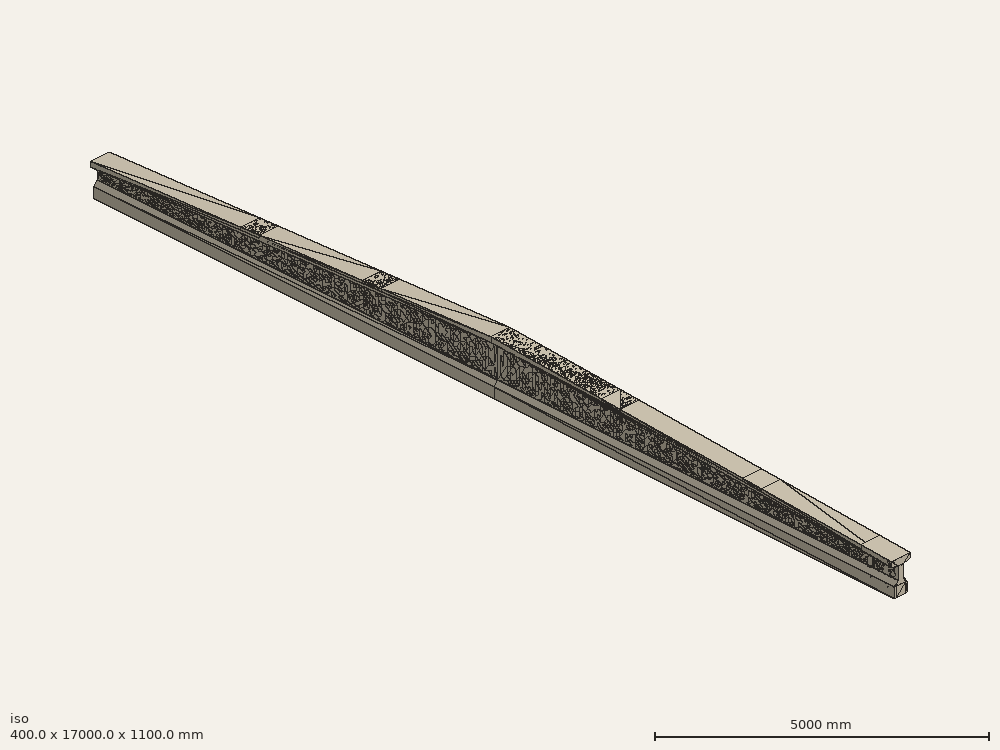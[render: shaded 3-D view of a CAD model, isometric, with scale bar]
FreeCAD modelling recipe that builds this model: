
FCSTD DOCUMENT  (FreeCAD 0.21R33694 (Git))
Label: LGH_3002_beam
License: All rights reserved
LicenseURL: http://en.wikipedia.org/wiki/All_rights_reserved
objects: Part::FeaturePython×24, Part::Feature×20, Part::Part2DObjectPython×9, Fem::ConstraintForce×9, Sketcher::SketchObject×6, App::MaterialObjectPython×4, Part::Extrusion×3, Part::Compound×3, Part::Mirroring×2, Fem::ConstraintDisplacement×2, Part::Loft×1, App::DocumentObjectGroup×1, Fem::FemSolverObjectPython×1, Fem::FemMeshObjectPython×1, Fem::FemAnalysis×1
note: 68 computed .brp shape members not serialized (recipe doc carries the construction recipe); baked Part::Feature solids carry a one-line shape summary decoded from their .brp

FEATURE [Sketcher::SketchObject] Sketch
  FullyConstrained = true
  Placement = pos=(0,0,0) rot=(1,0,0;1.5708rad)
  sketch-geometry (12):
    g0: LineSegment StartX=-130 StartY=0 StartZ=0 EndX=130 EndY=4e-16 EndZ=0
    g1: LineSegment StartX=130 StartY=4e-16 StartZ=0 EndX=130 EndY=200 EndZ=0
    g2: LineSegment StartX=130 StartY=200 StartZ=0 EndX=60 EndY=290 EndZ=0
    g3: LineSegment StartX=60 StartY=290 StartZ=0 EndX=60 EndY=540 EndZ=0
    g4: LineSegment StartX=60 StartY=540 StartZ=0 EndX=200 EndY=570 EndZ=0
    g5: LineSegment StartX=200 StartY=570 StartZ=0 EndX=200 EndY=670 EndZ=0
    g6: LineSegment StartX=200 StartY=670 StartZ=0 EndX=-200 EndY=670 EndZ=0
    g7: LineSegment StartX=-200 StartY=670 StartZ=0 EndX=-200 EndY=570 EndZ=0
    g8: LineSegment StartX=-200 StartY=570 StartZ=0 EndX=-60 EndY=540 EndZ=0
    g9: LineSegment StartX=-60 StartY=540 StartZ=0 EndX=-60 EndY=290 EndZ=0
    g10: LineSegment StartX=-60 StartY=290 StartZ=0 EndX=-130 EndY=200 EndZ=0
    g11: LineSegment StartX=-130 StartY=200 StartZ=0 EndX=-130 EndY=0 EndZ=0
  constraints (33):
    c: PointOnObject(g0,g-1)
    c: Symmetric(g0,g0,g-2)
    c: DistanceX(g0,g0) = 260
    c: Coincident(g0,g1)
    c: Vertical(g1)
    c: Coincident(g1,g2)
    c: Coincident(g2,g3)
    c: Vertical(g3)
    c: Coincident(g3,g4)
    c: Coincident(g4,g5)
    c: Vertical(g5)
    c: Coincident(g5,g6)
    c: Coincident(g6,g7)
    c: Vertical(g7)
    c: Coincident(g7,g8)
    c: Coincident(g8,g9)
    c: Vertical(g9)
    c: Coincident(g9,g10)
    c: Coincident(g10,g11)
    c: Coincident(g11,g0)
    c: Vertical(g11)
    c: Equal(g11,g1)
    c: Symmetric(g9,g2,g-2)
    c: Equal(g9,g3)
    c: Symmetric(g6,g5,g-2)
    c: DistanceX(g6,g6) = 400
    c: DistanceY(g0,g5) = 670
    c: Equal(g7,g5)
    c: DistanceX(g9,g2) = 120
    c: DistanceY(g5,g5) = 100
    c: DistanceY(g3,g4) = 30
    c: DistanceY(g1,g1) = 200
    c: DistanceY(g1,g2) = 90
FEATURE [Sketcher::SketchObject] Sketch001
  FullyConstrained = true
  Placement = pos=(0,8500,0) rot=(1,0,0;1.5708rad)
  sketch-geometry (12):
    g0: LineSegment StartX=-130 StartY=0 StartZ=0 EndX=130 EndY=0 EndZ=0
    g1: LineSegment StartX=130 StartY=0 StartZ=0 EndX=130 EndY=200 EndZ=0
    g2: LineSegment StartX=130 StartY=200 StartZ=0 EndX=60 EndY=290 EndZ=0
    g3: LineSegment StartX=60 StartY=290 StartZ=0 EndX=60 EndY=970 EndZ=0
    g4: LineSegment StartX=60 StartY=970 StartZ=0 EndX=200 EndY=1000 EndZ=0
    g5: LineSegment StartX=200 StartY=1000 StartZ=0 EndX=200 EndY=1100 EndZ=0
    g6: LineSegment StartX=200 StartY=1100 StartZ=0 EndX=-200 EndY=1100 EndZ=0
    g7: LineSegment StartX=-200 StartY=1100 StartZ=0 EndX=-200 EndY=1000 EndZ=0
    g8: LineSegment StartX=-200 StartY=1000 StartZ=0 EndX=-60 EndY=970 EndZ=0
    g9: LineSegment StartX=-60 StartY=970 StartZ=0 EndX=-60 EndY=290 EndZ=0
    g10: LineSegment StartX=-60 StartY=290 StartZ=0 EndX=-130 EndY=200 EndZ=0
    g11: LineSegment StartX=-130 StartY=200 StartZ=0 EndX=-130 EndY=0 EndZ=0
  constraints (33):
    c: PointOnObject(g0,g-1)
    c: Symmetric(g0,g0,g-2)
    c: DistanceX(g0,g0) = 260
    c: Coincident(g0,g1)
    c: Vertical(g1)
    c: Coincident(g1,g2)
    c: Coincident(g2,g3)
    c: Vertical(g3)
    c: Coincident(g3,g4)
    c: Coincident(g4,g5)
    c: Vertical(g5)
    c: Coincident(g5,g6)
    c: Coincident(g6,g7)
    c: Vertical(g7)
    c: Coincident(g7,g8)
    c: Coincident(g8,g9)
    c: Vertical(g9)
    c: Coincident(g9,g10)
    c: Coincident(g10,g11)
    c: Coincident(g11,g0)
    c: Vertical(g11)
    c: Equal(g11,g1)
    c: Symmetric(g9,g2,g-2)
    c: Equal(g9,g3)
    c: Symmetric(g6,g5,g-2)
    c: DistanceX(g6,g6) = 400
    c: DistanceY(g0,g5) = 1100
    c: Equal(g7,g5)
    c: DistanceX(g9,g2) = 120
    c: DistanceY(g5,g5) = 100
    c: DistanceY(g3,g4) = 30
    c: DistanceY(g1,g1) = 200
    c: DistanceY(g1,g2) = 90
FEATURE [Part::Loft] Loft
  Closed = false
  MaxDegree = 5
  Ruled = false
  Sections = -> [Sketch,Sketch001]
  Solid = true
FEATURE [Part::Part2DObjectPython] Rectangle  # Draft 2D object (typed FeaturePython)
  Area = 3.16759e+06
  ChamferSize = 0
  Columns = 1
  FilletRadius = 0
  Height = 1690
  Length = 1874.31
  MakeFace = true
  Placement = pos=(-1011.48,650,-530.33) rot=(1,0,0;1.5708rad)
  Rows = 1
FEATURE [Part::Feature] Loft001
  Placement = pos=(1.041e-12,17000,0) rot=(0,0,1;3.14159rad)
  shape: bbox 400 x 8500 x 1100 mm, 14 faces (baked)
FEATURE [Part::Feature] Loft002
  shape: bbox 400 x 8500 x 1100 mm, 14 faces (baked)
FEATURE [Part::FeaturePython] Slice  # WARN: FeaturePython — macro-defined, semantics opaque (R4)
  Base = -> Loft002
  Mode = 1
  Tolerance = 0
  Tools = -> [Rectangle]
FEATURE [Part::FeaturePython] Slice_child0  label="Slice.0"  # WARN: FeaturePython — macro-defined, semantics opaque (R4)
  Base = -> Slice
  FilterType = 1
  Invert = false
  OverrideMaxVal = 0
  WindowFrom = 80
  WindowTo = 100
  items = 0
FEATURE [Part::FeaturePython] Slice_child1  label="Slice.1"  # WARN: FeaturePython — macro-defined, semantics opaque (R4)
  Base = -> Slice
  FilterType = 1
  Invert = false
  OverrideMaxVal = 0
  WindowFrom = 80
  WindowTo = 100
  items = 1
FEATURE [App::DocumentObjectGroup] GrExplode_Slice  label="Exploded Slice"
  Group = -> [Slice_child0,Slice_child1]
FEATURE [Part::FeaturePython] Facebinder  # WARN: FeaturePython — macro-defined, semantics opaque (R4)
  Area = 150846
  Extrusion = 0
  Faces = -> [Slice_child1]
  RemoveSplitter = false
  Sew = false
FEATURE [Sketcher::SketchObject] Sketch002  label="Lage_Spannkabel"
  FullyConstrained = false
  MapMode = 5
  Placement = pos=(0,650,0) rot=(1,0,0;1.5708rad)
  Support = -> [Facebinder]
  sketch-geometry (2):
    g0: LineSegment StartX=0 StartY=0 StartZ=0 EndX=0 EndY=362 EndZ=0
    g1: LineSegment StartX=0 StartY=100 StartZ=0 EndX=947.371 EndY=100 EndZ=0
  constraints (6):
    c: Coincident(g0,g-1)
    c: Vertical(g0)
    c: DistanceY(g0,g0) = 362
    c: PointOnObject(g1,g0)
    c: Horizontal(g1)
    c: DistanceY(g1,g0) = 262
FEATURE [Sketcher::SketchObject] Sketch003
  ExternalGeometry = -> [Sketch002]
  FullyConstrained = true
  MapMode = 5
  Placement = pos=(0,0,0) rot=(1,0,0;1.5708rad)
  Support = -> [Loft]
  sketch-geometry (4):
    g0: LineSegment StartX=-100 StartY=200 StartZ=0 EndX=100 EndY=200 EndZ=0
    g1: LineSegment StartX=100 StartY=200 StartZ=0 EndX=100 EndY=0 EndZ=0
    g2: LineSegment StartX=100 StartY=0 StartZ=0 EndX=-100 EndY=0 EndZ=0
    g3: LineSegment StartX=-100 StartY=0 StartZ=0 EndX=-100 EndY=200 EndZ=0
  constraints (10):
    c: Coincident(g0,g1)
    c: Coincident(g1,g2)
    c: Coincident(g2,g3)
    c: Coincident(g3,g0)
    c: Horizontal(g0)
    c: Vertical(g3)
    c: Symmetric(g1,g0,g-3)
    c: Symmetric(g2,g1,g-2)
    c: DistanceX(g2,g2) = 200
    c: PointOnObject(g1,g-1)
FEATURE [Part::Extrusion] Extrude  label="Lager_links"
  Base = -> Sketch003
  Dir = (0,1,0)
  DirMode = 0
  FaceMakerClass = Part::FaceMakerBullseye
  LengthFwd = 200
  LengthRev = 0
  Solid = true
  Symmetric = false
FEATURE [Part::FeaturePython] Clone  label="Lager_rechts"  # Draft clone (typed FeaturePython)
  AttacherType = Attacher::AttachEngine3D
  Fuse = false
  Objects = -> [Extrude]
  Placement = pos=(1.0409e-12,16800,2e-16) rot=(0,0,1;0rad)
  Scale = (1,1,1)
FEATURE [Sketcher::SketchObject] Sketch004
  ExternalGeometry = -> [Loft]
  FullyConstrained = true
  MapMode = 5
  Placement = pos=(0,-33.8076,668.29) rot=(1,0,0;0.050545rad)
  Support = -> [Loft]
  sketch-geometry (12):
    g0: LineSegment StartX=-200 StartY=6200 StartZ=0 EndX=200 EndY=6200 EndZ=0
    g1: LineSegment StartX=200 StartY=6200 StartZ=0 EndX=200 EndY=5800 EndZ=0
    g2: LineSegment StartX=200 StartY=5800 StartZ=0 EndX=-200 EndY=5800 EndZ=0
    g3: LineSegment StartX=-200 StartY=5800 StartZ=0 EndX=-200 EndY=6200 EndZ=0
    g4: LineSegment StartX=-200 StartY=3200 StartZ=0 EndX=200 EndY=3200 EndZ=0
    g5: LineSegment StartX=200 StartY=3200 StartZ=0 EndX=200 EndY=2800 EndZ=0
    g6: LineSegment StartX=200 StartY=2800 StartZ=0 EndX=-200 EndY=2800 EndZ=0
    g7: LineSegment StartX=-200 StartY=2800 StartZ=0 EndX=-200 EndY=3200 EndZ=0
    g8: LineSegment StartX=-200 StartY=5800 StartZ=0 EndX=0 EndY=6000 EndZ=0
    g9: LineSegment StartX=0 StartY=6000 StartZ=0 EndX=200 EndY=6200 EndZ=0
    g10: LineSegment StartX=-200 StartY=2800 StartZ=0 EndX=0 EndY=3000 EndZ=0
    g11: LineSegment StartX=0 StartY=3000 StartZ=0 EndX=200 EndY=3200 EndZ=0
  constraints (32):
    c: Coincident(g0,g1)
    c: Coincident(g1,g2)
    c: Coincident(g2,g3)
    c: Coincident(g3,g0)
    c: Horizontal(g0)
    c: Vertical(g1)
    c: Vertical(g3)
    c: Coincident(g4,g5)
    c: Coincident(g5,g6)
    c: Coincident(g6,g7)
    c: Coincident(g7,g4)
    c: Horizontal(g4)
    c: Vertical(g5)
    c: Vertical(g7)
    c: Symmetric(g2,g1,g-2)
    c: DistanceX(g2,g2) = 400
    c: Symmetric(g6,g5,g-2)
    c: Equal(g2,g6)
    c: Coincident(g2,g8)
    c: PointOnObject(g8,g-2)
    c: Coincident(g8,g9)
    c: Coincident(g9,g0)
    c: Coincident(g6,g10)
    c: PointOnObject(g10,g-2)
    c: Coincident(g11,g10)
    c: Coincident(g11,g4)
    c: Parallel(g10,g11)
    c: Equal(g6,g5)
    c: Parallel(g8,g9)
    c: Equal(g2,g1)
    c: DistanceY(g10,g8) = 3000
    c: DistanceY(g-1,g10) = 3000
FEATURE [Part::Extrusion] Extrude001  label="Auflager_Mast"
  Base = -> Sketch004
  Dir = (0,-0.0505236,0.998723)
  DirMode = 2
  FaceMakerClass = Part::FaceMakerBullseye
  LengthFwd = 50
  LengthRev = 0
  Reversed = true
  Solid = true
  Symmetric = false
FEATURE [Sketcher::SketchObject] Sketch005
  ExternalGeometry = -> [Extrude001,Loft001]
  FullyConstrained = true
  MapMode = 5
  Placement = pos=(1.041e-12,17033.8,668.29) rot=(0,0.02527,0.999681;3.14159rad)
  Support = -> [Loft001]
  sketch-geometry (8):
    g0: LineSegment StartX=-200 StartY=3227.29 StartZ=0 EndX=200 EndY=3227.29 EndZ=0
    g1: LineSegment StartX=200 StartY=3227.29 StartZ=0 EndX=200 EndY=3627.29 EndZ=0
    g2: LineSegment StartX=200 StartY=3627.29 StartZ=0 EndX=-200 EndY=3627.29 EndZ=0
    g3: LineSegment StartX=-200 StartY=3627.29 StartZ=0 EndX=-200 EndY=3227.29 EndZ=0
    g4: LineSegment StartX=-200 StartY=6211.97 StartZ=0 EndX=200 EndY=6211.97 EndZ=0
    g5: LineSegment StartX=200 StartY=6211.97 StartZ=0 EndX=200 EndY=5811.97 EndZ=0
    g6: LineSegment StartX=200 StartY=5811.97 StartZ=0 EndX=-200 EndY=5811.97 EndZ=0
    g7: LineSegment StartX=-200 StartY=5811.97 StartZ=0 EndX=-200 EndY=6211.97 EndZ=0
  constraints (22):
    c: Coincident(g0,g1)
    c: Coincident(g1,g2)
    c: Coincident(g2,g3)
    c: Coincident(g3,g0)
    c: Horizontal(g0)
    c: Horizontal(g2)
    c: Vertical(g1)
    c: Vertical(g3)
    c: Coincident(g4,g5)
    c: Coincident(g5,g6)
    c: Coincident(g6,g7)
    c: Coincident(g7,g4)
    c: Horizontal(g4)
    c: Horizontal(g6)
    c: Vertical(g5)
    c: Vertical(g7)
    c: Symmetric(g0,g-3,g-5)
    c: Vertical(g0,g-5)
    c: Vertical(g-5,g4)
    c: Symmetric(g4,g-4,g-5)
    c: Equal(g6,g7)
    c: Equal(g7,g3)
FEATURE [Part::Extrusion] Extrude002  label="Auflager_dummy"
  Base = -> Sketch005
  Dir = (0,0.0505236,0.998723)
  DirMode = 2
  FaceMakerClass = Part::FaceMakerBullseye
  LengthFwd = 50
  LengthRev = 0
  Reversed = true
  Solid = true
  Symmetric = false
FEATURE [Fem::FemSolverObjectPython] SolverCcxTools  # FEM object (typed FeaturePython)
  AnalysisType = 0
  BeamShellResultOutput3D = true
  BucklingFactors = 1
  EigenmodeHighLimit = 1000000
  EigenmodeLowLimit = 0
  EigenmodesCount = 10
  GeometricalNonlinearity = 0
  IterationsControlParameterCutb = 0.25,0.5,0.75,0.85,,,1.5,
  IterationsControlParameterIter = 4,8,9,200,10,400,,200,,
  IterationsControlParameterTimeUse = false
  IterationsThermoMechMaximum = 2000
  IterationsUserDefinedIncrementations = false
  IterationsUserDefinedTimeStepLength = false
  MaterialNonlinearity = 0
  MatrixSolverType = 0
  SplitInputWriter = true
  ThermoMechSteadyState = true
  TimeEnd = 1
  TimeInitialStep = 0.01
FEATURE [Part::FeaturePython] Slice001  # WARN: FeaturePython — macro-defined, semantics opaque (R4)
  Base = -> Loft
  Mode = 1
  Tolerance = 0
  Tools = -> [Extrude,Extrude001]
FEATURE [Part::FeaturePython] Slice001_child0  label="Slice001.0"  # WARN: FeaturePython — macro-defined, semantics opaque (R4)
  Base = -> Slice001
  FilterType = 1
  Invert = false
  OverrideMaxVal = 0
  WindowFrom = 80
  WindowTo = 100
  items = 0
FEATURE [Part::FeaturePython] Slice001_child1  label="Slice001.1"  # WARN: FeaturePython — macro-defined, semantics opaque (R4)
  Base = -> Slice001
  FilterType = 1
  Invert = false
  OverrideMaxVal = 0
  WindowFrom = 80
  WindowTo = 100
  items = 1
FEATURE [Part::FeaturePython] Slice001_child2  label="Slice001.2"  # WARN: FeaturePython — macro-defined, semantics opaque (R4)
  Base = -> Slice001
  FilterType = 1
  Invert = false
  OverrideMaxVal = 0
  WindowFrom = 80
  WindowTo = 100
  items = 2
FEATURE [Part::FeaturePython] Slice001_child3  label="Slice001.3"  # WARN: FeaturePython — macro-defined, semantics opaque (R4)
  Base = -> Slice001
  FilterType = 1
  Invert = false
  OverrideMaxVal = 0
  WindowFrom = 80
  WindowTo = 100
  items = 3
FEATURE [Part::FeaturePython] Slice002  # WARN: FeaturePython — macro-defined, semantics opaque (R4)
  Base = -> Loft001
  Mode = 1
  Tolerance = 0
  Tools = -> [Clone,Extrude002]
FEATURE [Part::FeaturePython] Slice002_child0  label="Slice002.0"  # WARN: FeaturePython — macro-defined, semantics opaque (R4)
  Base = -> Slice002
  FilterType = 1
  Invert = false
  OverrideMaxVal = 0
  WindowFrom = 80
  WindowTo = 100
  items = 0
FEATURE [Part::FeaturePython] Slice002_child1  label="Slice002.1"  # WARN: FeaturePython — macro-defined, semantics opaque (R4)
  Base = -> Slice002
  FilterType = 1
  Invert = false
  OverrideMaxVal = 0
  WindowFrom = 80
  WindowTo = 100
  items = 1
FEATURE [Part::FeaturePython] Slice002_child2  label="Slice002.2"  # WARN: FeaturePython — macro-defined, semantics opaque (R4)
  Base = -> Slice002
  FilterType = 1
  Invert = false
  OverrideMaxVal = 0
  WindowFrom = 80
  WindowTo = 100
  items = 2
FEATURE [Part::FeaturePython] Slice002_child3  label="Slice002.3"  # WARN: FeaturePython — macro-defined, semantics opaque (R4)
  Base = -> Slice002
  FilterType = 1
  Invert = false
  OverrideMaxVal = 0
  WindowFrom = 80
  WindowTo = 100
  items = 3
FEATURE [Part::Feature] Solid
  shape: bbox 400 x 8500 x 1100 mm, 26 faces (baked)
FEATURE [Part::Feature] Solid001  label="support_left"
  shape: bbox 200 x 200 x 200 mm, 6 faces (baked)
FEATURE [Part::Feature] Solid002  label="pad2"
  shape: bbox 400 x 8500 x 530 mm, 6 faces (baked)
FEATURE [Part::Feature] Solid003  label="pad1"
  shape: bbox 400 x 8500 x 530 mm, 6 faces (baked)
FEATURE [Fem::ConstraintForce] ConstraintForce005  label="steelframe_self(p)"
  DirectionVector = (0,0.0505236,-0.998723)
  Force = 1700
  NormalDirection = (0,-0.0505236,0.998723)
  Points = (16) [(200,2762.62,809.756),(66.6667,2762.62,809.756),(-66.6667,2762.62,809.756),(-200,2762.62,809.756),(200,2895.78,816.492),(66.6667,2895.78,816.492),+10 more]
  References = -> [Solid003]
  Reversed = true
  Scale = 22
  expr: Force = 1700
FEATURE [Fem::ConstraintForce] ConstraintForce006  label="steelframe_wind(v)"
  DirectionVector = (0,0.0505236,-0.998723)
  Force = 5500
  NormalDirection = (0,-0.0505236,0.998723)
  Points = (16) [(200,2762.62,809.756),(66.6667,2762.62,809.756),(-66.6667,2762.62,809.756),(-200,2762.62,809.756),(200,2895.78,816.492),(66.6667,2895.78,816.492),+10 more]
  References = -> [Solid003]
  Reversed = true
  Scale = 22
FEATURE [Part::Feature] Solid004
  shape: bbox 400 x 8500 x 1100 mm, 26 faces (baked)
FEATURE [Part::Feature] Solid005  label="support_right"
  shape: bbox 200 x 200 x 200 mm, 6 faces (baked)
FEATURE [Part::Feature] Solid006  label="pad3"
  shape: bbox 400 x 8500 x 530 mm, 6 faces (baked)
FEATURE [Part::Feature] Solid007  label="pad4"
  shape: bbox 400 x 8500 x 530 mm, 6 faces (baked)
FEATURE [Part::Compound] Compound  label="slices"
  Links = -> [Slice001_child0,Slice001_child1,Slice001_child2,Slice001_child3,Slice002_child0,Slice002_child1,Slice002_child2,Slice002_child3]
FEATURE [Part::Part2DObjectPython] Line  # Draft 2D object (typed FeaturePython)
  Area = 0
  ChamferSize = 0
  Closed = false
  End = (60,8500,970)
  FilletRadius = 0
  Length = 120
  MakeFace = true
  Placement = pos=(-60,8500,970) rot=(0.819793,0.571689,-0.033324;1.73245rad)
  Points = (2) [(0,0,0),(74.3136,69.2385,63.9025)]
  Start = (-60,8500,970)
  Subdivisions = 0
FEATURE [Part::Part2DObjectPython] Line001  # Draft 2D object (typed FeaturePython)
  Area = 0
  ChamferSize = 0
  Closed = false
  End = (60,17000,540)
  FilletRadius = 0
  Length = 8510.87
  MakeFace = true
  Placement = pos=(60,8500,970) rot=(0.819793,0.571689,-0.033324;1.73245rad)
  Points = (2) [(0,0,0),(4601.54,1518.69,-6996.74)]
  Start = (60,8500,970)
  Subdivisions = 0
FEATURE [Part::Part2DObjectPython] Line002  # Draft 2D object (typed FeaturePython)
  Area = 0
  ChamferSize = 0
  Closed = false
  End = (-60,17000,540)
  FilletRadius = 0
  Length = 120
  MakeFace = true
  Placement = pos=(60,17000,540) rot=(0.316109,0.658255,0.683209;2.4861rad)
  Points = (2) [(0,0,0),(73.6331,5.20958,-94.6099)]
  Start = (60,17000,540)
  Subdivisions = 0
FEATURE [Part::Part2DObjectPython] Line003  # Draft 2D object (typed FeaturePython)
  Area = 0
  ChamferSize = 0
  Closed = false
  End = (-60,8500,970)
  FilletRadius = 0
  Length = 8510.87
  MakeFace = true
  Placement = pos=(-60,17000,540) rot=(-0.233099,0.743064,0.627312;3.31022rad)
  Points = (2) [(0,0,0),(3747.29,-525.601,-7623.42)]
  Start = (-60,17000,540)
  Subdivisions = 0
FEATURE [Part::Feature] Face
  shape: bbox 132 x 9350 x 473 mm, 1 faces, 0 solids (baked)
FEATURE [Part::Part2DObjectPython] Line004  # Draft 2D object (typed FeaturePython)
  Area = 0
  ChamferSize = 0
  Closed = false
  End = (-60,17000,290)
  FilletRadius = 0
  Length = 120
  MakeFace = true
  Placement = pos=(60,17000,290) rot=(0.094723,0.678944,0.728054;2.81253rad)
  Points = (2) [(0,0,0),(111.466,13.2123,-42.4359)]
  Start = (60,17000,290)
  Subdivisions = 0
FEATURE [Part::Part2DObjectPython] Line005  # Draft 2D object (typed FeaturePython)
  Area = 0
  ChamferSize = 0
  Closed = false
  End = (-60,8500,290)
  FilletRadius = 0
  Length = 8500
  MakeFace = true
  Placement = pos=(-60,17000,290) rot=(0.929676,0.114122,-0.350256;1.59671rad)
  Points = (2) [(0,0,0),(2050.99,106.63,8248.16)]
  Start = (-60,17000,290)
  Subdivisions = 0
FEATURE [Part::Part2DObjectPython] Line006  # Draft 2D object (typed FeaturePython)
  Area = 0
  ChamferSize = 0
  Closed = false
  End = (60,8500,290)
  FilletRadius = 0
  Length = 120
  MakeFace = true
  Placement = pos=(-60,8500,290) rot=(0.929676,0.114122,-0.350256;1.59671rad)
  Points = (2) [(0,0,0),(103.294,55.0781,-26.3971)]
  Start = (-60,8500,290)
  Subdivisions = 0
FEATURE [Part::Part2DObjectPython] Line007  # Draft 2D object (typed FeaturePython)
  Area = 0
  ChamferSize = 0
  Closed = false
  End = (60,17000,290)
  FilletRadius = 0
  Length = 8500
  MakeFace = true
  Placement = pos=(60,8500,290) rot=(0.895286,0.437229,-0.085401;1.72603rad)
  Points = (2) [(0,0,0),(3124.52,562.012,-7884.89)]
  Start = (60,8500,290)
  Subdivisions = 0
FEATURE [Part::Feature] Face001
  shape: bbox 132 x 9350 x 2.016e-07 mm, 1 faces, 0 solids (baked)
FEATURE [Part::Mirroring] Part__Mirroring  label="Face (Mirror #1)"
  Base = (0,8500,290)
  Normal = (0,1,0)
  Source = -> Face
FEATURE [Part::Mirroring] Part__Mirroring001  label="Face001 (Mirror #2)"
  Base = (0,8500,290)
  Normal = (0,1,0)
  Source = -> Face001
FEATURE [Part::Feature] Face002
  shape: bbox 132 x 9350 x 473 mm, 1 faces, 0 solids (baked)
FEATURE [Part::Feature] Face003
  shape: bbox 132 x 9350 x 2.016e-07 mm, 1 faces, 0 solids (baked)
FEATURE [Part::FeaturePython] Slice003  # WARN: FeaturePython — macro-defined, semantics opaque (R4)
  Base = -> Solid004
  Mode = 1
  Tolerance = 0
  Tools = -> [Face002,Face003]
FEATURE [Part::FeaturePython] Slice003_child0  label="Slice003.0"  # WARN: FeaturePython — macro-defined, semantics opaque (R4)
  Base = -> Slice003
  FilterType = 1
  Invert = false
  OverrideMaxVal = 0
  WindowFrom = 80
  WindowTo = 100
  items = 0
FEATURE [Part::FeaturePython] Slice003_child1  label="Slice003.1"  # WARN: FeaturePython — macro-defined, semantics opaque (R4)
  Base = -> Slice003
  FilterType = 1
  Invert = false
  OverrideMaxVal = 0
  WindowFrom = 80
  WindowTo = 100
  items = 1
FEATURE [Part::FeaturePython] Slice003_child2  label="Slice003.2"  # WARN: FeaturePython — macro-defined, semantics opaque (R4)
  Base = -> Slice003
  FilterType = 1
  Invert = false
  OverrideMaxVal = 0
  WindowFrom = 80
  WindowTo = 100
  items = 2
FEATURE [Part::FeaturePython] Slice004  # WARN: FeaturePython — macro-defined, semantics opaque (R4)
  Base = -> Solid
  Mode = 1
  Tolerance = 0
  Tools = -> [Part__Mirroring,Part__Mirroring001]
FEATURE [Part::FeaturePython] Slice004_child0  label="Slice004.0"  # WARN: FeaturePython — macro-defined, semantics opaque (R4)
  Base = -> Slice004
  FilterType = 1
  Invert = false
  OverrideMaxVal = 0
  WindowFrom = 80
  WindowTo = 100
  items = 0
FEATURE [Part::FeaturePython] Slice004_child1  label="Slice004.1"  # WARN: FeaturePython — macro-defined, semantics opaque (R4)
  Base = -> Slice004
  FilterType = 1
  Invert = false
  OverrideMaxVal = 0
  WindowFrom = 80
  WindowTo = 100
  items = 1
FEATURE [Part::FeaturePython] Slice004_child2  label="Slice004.2"  # WARN: FeaturePython — macro-defined, semantics opaque (R4)
  Base = -> Slice004
  FilterType = 1
  Invert = false
  OverrideMaxVal = 0
  WindowFrom = 80
  WindowTo = 100
  items = 2
FEATURE [Part::Feature] Solid008  label="bottom_flange_right"
  shape: bbox 260 x 9350 x 290 mm, 12 faces (baked)
FEATURE [Part::Feature] Solid009  label="web_right"
  shape: bbox 132 x 9350 x 701.5 mm, 6 faces (baked)
FEATURE [Part::Feature] Solid010  label="top_flange_right"
  shape: bbox 400 x 9350 x 581.5 mm, 16 faces (baked)
FEATURE [Part::Feature] Solid011  label="bottom_flange_left"
  shape: bbox 260 x 9350 x 290 mm, 12 faces (baked)
FEATURE [Part::Feature] Solid012  label="web_left"
  shape: bbox 132 x 9350 x 701.5 mm, 6 faces (baked)
FEATURE [Part::Feature] Solid013  label="top_flange_left"
  shape: bbox 400 x 9350 x 581.5 mm, 16 faces (baked)
FEATURE [Part::Compound] Compound001  label="slices_001"
  Links = -> [Slice003_child0,Slice003_child1,Slice003_child2,Slice004_child0,Slice004_child1,Slice004_child2]
FEATURE [Part::Compound] Compound002  label="lines"
  Links = -> [Line,Line001,Line002,Line003,Line004,Line005,Line006,Line007]
FEATURE [App::MaterialObjectPython] MaterialSolid  label="bottom_flange"  # material (typed FeaturePython)
  Category = 0
  Material = AngleOfFriction=30 deg,AuthorAndLicense=(c) 2019 Bernd Hahnebach (CC-BY 3.0),CardName=Concrete-EN-C35_45,CompressiveStrength=15.75 MPa,+7 more (map truncated)
  References = -> [Solid011,Solid008]
FEATURE [App::MaterialObjectPython] MaterialSolid001  label="top_flange"  # material (typed FeaturePython)
  Category = 0
  Material = AngleOfFriction=30 deg,AuthorAndLicense=(c) 2019 Bernd Hahnebach (CC-BY 3.0),CardName=Concrete-EN-C35_45,CompressiveStrength=15.75 MPa,+7 more (map truncated)
  References = -> [Solid013,Solid003,Solid002,Solid010,Solid006,Solid007]
FEATURE [App::MaterialObjectPython] MaterialSolid002  label="web"  # material (typed FeaturePython)
  Category = 0
  Material = AngleOfFriction=30 deg,AuthorAndLicense=(c) 2019 Bernd Hahnebach (CC-BY 3.0),CardName=Concrete-EN-C35_45,CompressiveStrength=15.75 MPa,+7 more (map truncated)
  References = -> [Solid012,Solid009]
FEATURE [App::MaterialObjectPython] MaterialSolid003  label="supports"  # material (typed FeaturePython)
  Category = 0
  Material = AngleOfFriction=30 deg,AuthorAndLicense=(c) 2019 Bernd Hahnebach (CC-BY 3.0),CardName=Concrete-EN-C35_45,CompressiveStrength=15.75 MPa,+7 more (map truncated)
  References = -> [Solid001,Solid005]
FEATURE [Part::FeaturePython] BooleanFragments  # WARN: FeaturePython — macro-defined, semantics opaque (R4)
  Mode = 2
  Objects = -> [Solid001,Solid002,Solid003,Solid005,Solid006,Solid007,Solid008,Solid009,Solid010,Solid011,Solid012,Solid013]
  Tolerance = 0
FEATURE [Fem::ConstraintDisplacement] ConstraintDisplacement  label="left_support"
  NormalDirection = (0,0,-1)
  Normals = (4) [(0,0,-1),(0,0,-1),(0,0,-1),(0,0,-1)]
  Points = (4) [(-100,0,0),(-33.3333,0,0),(33.3333,0,0),(100,0,0)]
  References = -> [BooleanFragments]
  Scale = 15
  hasXFormula = false
  hasYFormula = false
  hasZFormula = false
  rotxFix = false
  rotxFree = true
  rotyFix = false
  rotyFree = true
  rotzFix = false
  rotzFree = true
  useFlowSurfaceForce = false
  xDisplacement = 0
  xFix = true
  xFree = false
  xRotation = 0
  yDisplacement = 0
  yFix = true
  yFree = false
  yRotation = 0
  zDisplacement = 0
  zFix = true
  zFree = false
  zRotation = 0
FEATURE [Fem::ConstraintDisplacement] ConstraintDisplacement001  label="right_support"
  NormalDirection = (0,1,-2e-16)
  Normals = (4) [(0,1,-2e-16),(0,1,-2e-16),(0,1,-2e-16),(0,1,-2e-16)]
  Points = (4) [(100,17000,0),(33.3333,17000,0),(-33.3333,17000,0),(-100,17000,0)]
  References = -> [BooleanFragments]
  Scale = 15
  hasXFormula = false
  hasYFormula = false
  hasZFormula = false
  rotxFix = false
  rotxFree = true
  rotyFix = false
  rotyFree = true
  rotzFix = false
  rotzFree = true
  useFlowSurfaceForce = false
  xDisplacement = 0
  xFix = true
  xFree = false
  xRotation = 0
  yDisplacement = 0
  yFix = false
  yFree = true
  yRotation = 0
  zDisplacement = 0
  zFix = true
  zFree = false
  zRotation = 0
FEATURE [Fem::ConstraintForce] ConstraintForce  label="G_roof(p)"
  DirectionVector = (0,0.0505236,-0.998723)
  Force = 127500
  NormalDirection = (0,-0.0505236,0.998723)
  Points = (248) [(200,0,670),(66.6667,0,670),(-66.6667,0,670),(-200,0,670),(200,394.659,689.965),(66.6667,394.659,689.965),(-66.6667,394.659,689.965),+241 more]
  References = -> [BooleanFragments]
  Reversed = true
  Scale = 42
FEATURE [Fem::ConstraintForce] ConstraintForce001  label="Snow_roof(p)"
  DirectionVector = (0,0.0505236,-0.998723)
  Force = 86700
  NormalDirection = (0,-0.0505236,0.998723)
  Points = (248) [(200,0,670),(66.6667,0,670),(-66.6667,0,670),(-200,0,670),(200,394.659,689.965),(66.6667,394.659,689.965),(-66.6667,394.659,689.965),+241 more]
  References = -> [BooleanFragments]
  Reversed = true
  Scale = 42
FEATURE [Fem::ConstraintForce] ConstraintForce002  label="prestress1(p)"
  DirectionVector = (0,1,-2e-16)
  Force = 900000
  NormalDirection = (0,-1,2e-16)
  Points = (4) [(20.3179,8.85311e-15,40.2414),(59.7586,2.64699e-14,120.318),(-59.7586,1.75301e-14,79.6821),(-20.3179,3.51469e-14,159.759)]
  References = -> [BooleanFragments]
  Reversed = true
  Scale = 17
FEATURE [Fem::ConstraintForce] ConstraintForce003  label="prestress2(p)"
  DirectionVector = (0,-1,2e-16)
  Force = 900000
  NormalDirection = (0,1,-2e-16)
  Points = (4) [(-20.3179,17000,40.2414),(-59.7586,17000,120.318),(59.7586,17000,79.6821),(20.3179,17000,159.759)]
  References = -> [BooleanFragments]
  Reversed = true
  Scale = 17
FEATURE [Fem::ConstraintForce] ConstraintForce007  label="reaction(p)"
  DirectionVector = (0,0,1)
  Force = 289297
  NormalDirection = (0,0,-1)
  Points = (32) [(-100,0,0),(-33.3333,0,0),(33.3333,0,0),(100,0,0),(-100,66.6667,0),(-33.3333,66.6667,0),(33.3333,66.6667,0),(100,66.6667,0),(-100,133.333,0),+23 more]
  References = -> [BooleanFragments]
  Reversed = true
  Scale = 15
FEATURE [Fem::ConstraintForce] ConstraintForce008  label="reaction_left(v)"
  DirectionVector = (0,0,1)
  Force = 4529
  NormalDirection = (0,0,-1)
  Points = (16) [(-100,0,0),(-33.3333,0,0),(33.3333,0,0),(100,0,0),(-100,66.6667,0),(-33.3333,66.6667,0),(33.3333,66.6667,0),(100,66.6667,0),(-100,133.333,0),+7 more]
  References = -> [BooleanFragments]
  Reversed = true
  Scale = 15
FEATURE [Fem::ConstraintForce] ConstraintForce009  label="reaction_right(v)"
  DirectionVector = (0,0,1)
  Force = 971
  NormalDirection = (0,0,-1)
  Points = (16) [(100,17000,0),(33.3333,17000,0),(-33.3333,17000,0),(-100,17000,0),(100,16933.3,0),(33.3333,16933.3,0),(-33.3333,16933.3,0),(-100,16933.3,0),+8 more]
  References = -> [BooleanFragments]
  Reversed = true
  Scale = 15
FEATURE [Fem::FemMeshObjectPython] FEMMeshGmsh  # FEM object (typed FeaturePython)
  Algorithm2D = 0
  Algorithm3D = 0
  CharacteristicLengthMax = 0
  CharacteristicLengthMin = 0
  CoherenceMesh = true
  ElementDimension = 0
  ElementOrder = 1
  GeometryTolerance = 1e-06
  GroupsOfNodes = false
  HighOrderOptimize = 0
  MeshSizeFromCurvature = 12
  OptimizeNetgen = false
  OptimizeStd = true
  Part = -> BooleanFragments
  RecombinationAlgorithm = 0
  Recombine3DAll = false
  RecombineAll = false
  SecondOrderLinear = false
FEATURE [Fem::FemAnalysis] Analysis
  Group = -> [SolverCcxTools,ConstraintDisplacement,ConstraintDisplacement001,ConstraintForce,ConstraintForce001,ConstraintForce002,ConstraintForce003,ConstraintForce005,ConstraintForce006,ConstraintForce007,ConstraintForce008,ConstraintForce009,MaterialSolid,MaterialSolid001,MaterialSolid002,MaterialSolid003,FEMMeshGmsh]
